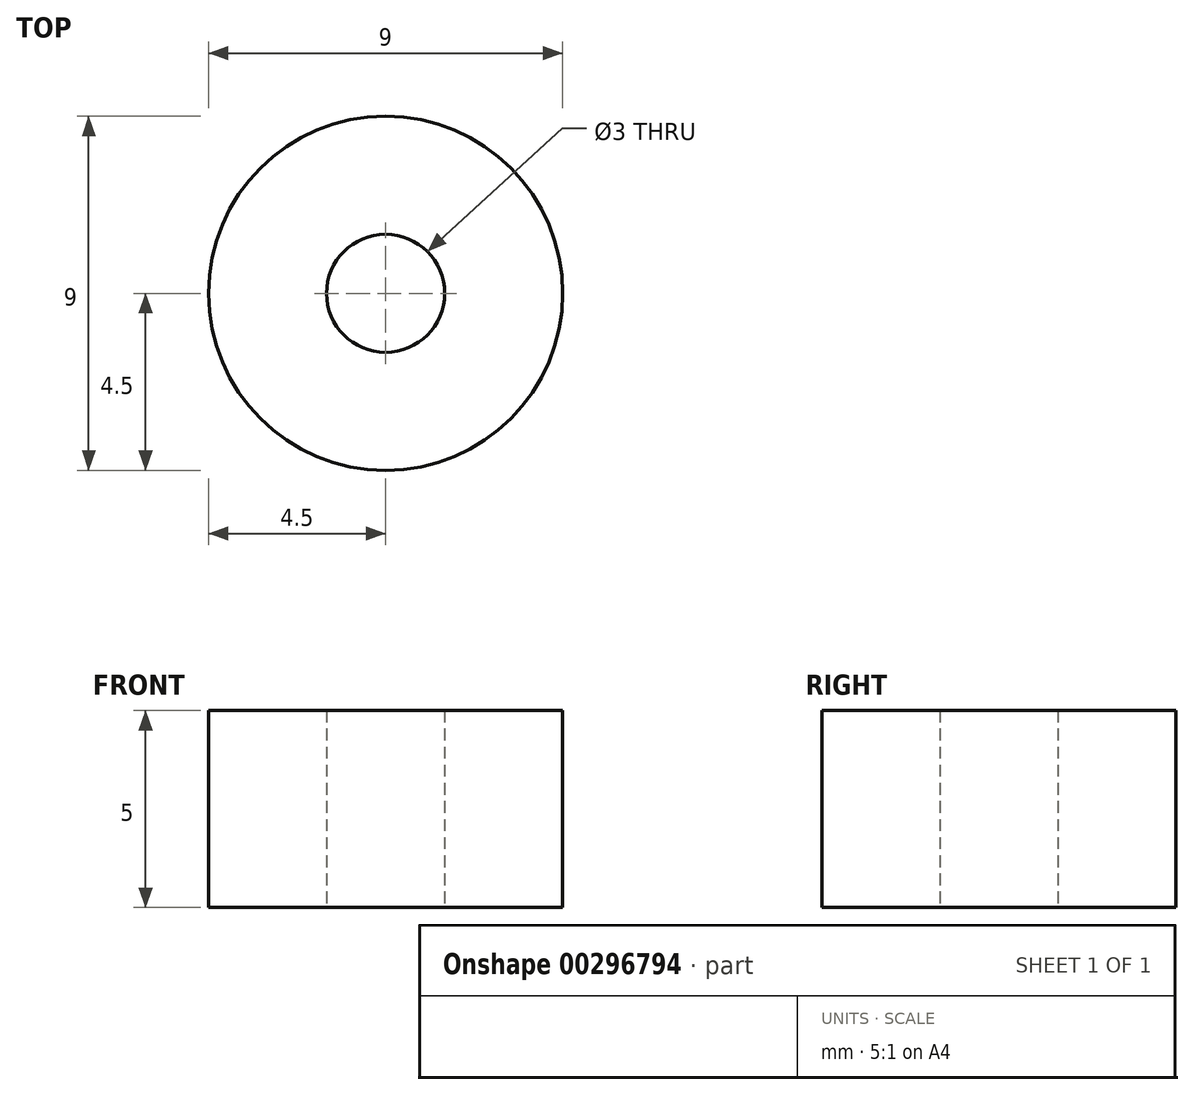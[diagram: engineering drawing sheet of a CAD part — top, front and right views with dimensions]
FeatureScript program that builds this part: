
annotation { "Feature Type Name" : "Feature", "Feature Type Description" : "" }
export const myFeature = defineFeature(function(context is Context, id is Id, definition is map)
    precondition{}
    {
        {
            var Q0;
            Q0=qCreatedBy(makeId("Top.planeOp"),FACE);
            var sketch = newSketch(context, id + "F0", { "sketchPlane" : qUnion([Q0])});
            skCircle(sketch, "E0", {"center": v(0, 0) * mm, "radius": 4.5 * mm});
            skCircle(sketch, "E1", {"center": v(0, 0) * mm, "radius": 1.5 * mm});
            skSolve(sketch);
        }
        {
            var Q0;
            Q0=makeQuery(id+"F0.imprint","IMPRINT",FACE,{"disambiguationData":[TD([[makeQuery(id+"F0.imprint","IMPRINT",EDGE,{"derivedFrom":sQuery(id+"F0.wireOp",EDGE,"E0")}),1.0]])]});
            extrude(context, id + "F1", {"entities" : qUnion([Q0]), "depth" : 5 * mm});
        }
    });
